# Revit family: 20 SMARTBACK
name_source: partatom
category: Furniture
units: mm (PartAtom-declared; Revit-internal decimal feet)

## family parameters
Always vertical = Yes
Cut with Voids When Loaded = No
Room Calculation Point = Yes
Shared = No
Work Plane-Based = Yes

## types (19) — shared parameters
Default Elevation = 1219 mm

## per-type parameters (varying)
| type | Armstand_00 | Armstand_01 | Armstand_02 | Armstand_03 | Base_00 | Base_01 | Headrest_00 | Seat_00 | Structure_00 | Synchron_00 | Synchron_01 | stand |
| PK 1_4PKGI02 | No | No | No | No | Yes | No | No | Seat_00 | Structure_00 | No | Yes | No |
| PK 1_4PKGI04 | No | No | No | No | Yes | No | No | Seat_00 | Structure_00 | No | Yes | No |
| PK 1_4PKGI06 | No | No | No | No | No | Yes | No | Seat_00 | Structure_00 | No | Yes | No |
| PK 1_4PKGI08 | No | No | No | No | No | Yes | No | <By Category> | <By Category> | No | Yes | No |
| PK 2_4PKGI10 | Yes | No | No | No | Yes | No | No | Seat_00 | Structure_00 | No | Yes | Yes |
| PK 2_4PKGI12 | Yes | No | No | No | Yes | No | No | Seat_00 | Structure_00 | No | Yes | Yes |
| PK 2_4PKGI14 | Yes | No | No | No | No | Yes | No | Seat_00 | Structure_00 | No | Yes | Yes |
| PK 2_4PKGI16 | Yes | No | No | No | No | Yes | No | Seat_00 | Structure_00 | No | Yes | Yes |
| PK 3_4PKGI18 | No | Yes | No | No | Yes | No | No | Seat_00 | Structure_00 | No | Yes | Yes |
| PK 3_4PKGI20 | No | Yes | No | No | Yes | No | No | Seat_00 | Structure_00 | No | Yes | Yes |
| PK 3_4PKGI22 | No | Yes | No | No | No | Yes | No | Seat_00 | Structure_00 | No | Yes | Yes |
| PK 3_4PKGI24 | No | Yes | No | No | No | Yes | No | Seat_00 | Structure_00 | No | Yes | Yes |
| PK 4_4PKGI26 | No | No | Yes | No | Yes | No | No | Seat_00 | Structure_00 | No | Yes | Yes |
| PK 4_4PKGI28 | No | No | Yes | No | Yes | No | No | Seat_00 | Structure_00 | Yes | No | Yes |
| PK 4_4PKGI30 | No | No | Yes | No | No | Yes | No | Seat_00 | Structure_00 | Yes | No | Yes |
| PK 4_4PKGI32 | No | No | Yes | No | No | Yes | No | Seat_00 | Structure_00 | Yes | No | Yes |
| PK10_4PKGI40 | No | No | No | No | Yes | No | No | Seat_00 | Structure_00 | Yes | No | No |
| PK11_4PKGI42 | No | No | Yes | No | Yes | No | No | Seat_00 | Structure_00 | Yes | No | Yes |
| PK12_4PKGI44 | No | No | No | Yes | Yes | No | Yes | Seat_00 | Structure_00 | Yes | No | No |

## geometry (parser evidence)
native form markers: Sweep x2
no freeform markers — native parametric forms only
